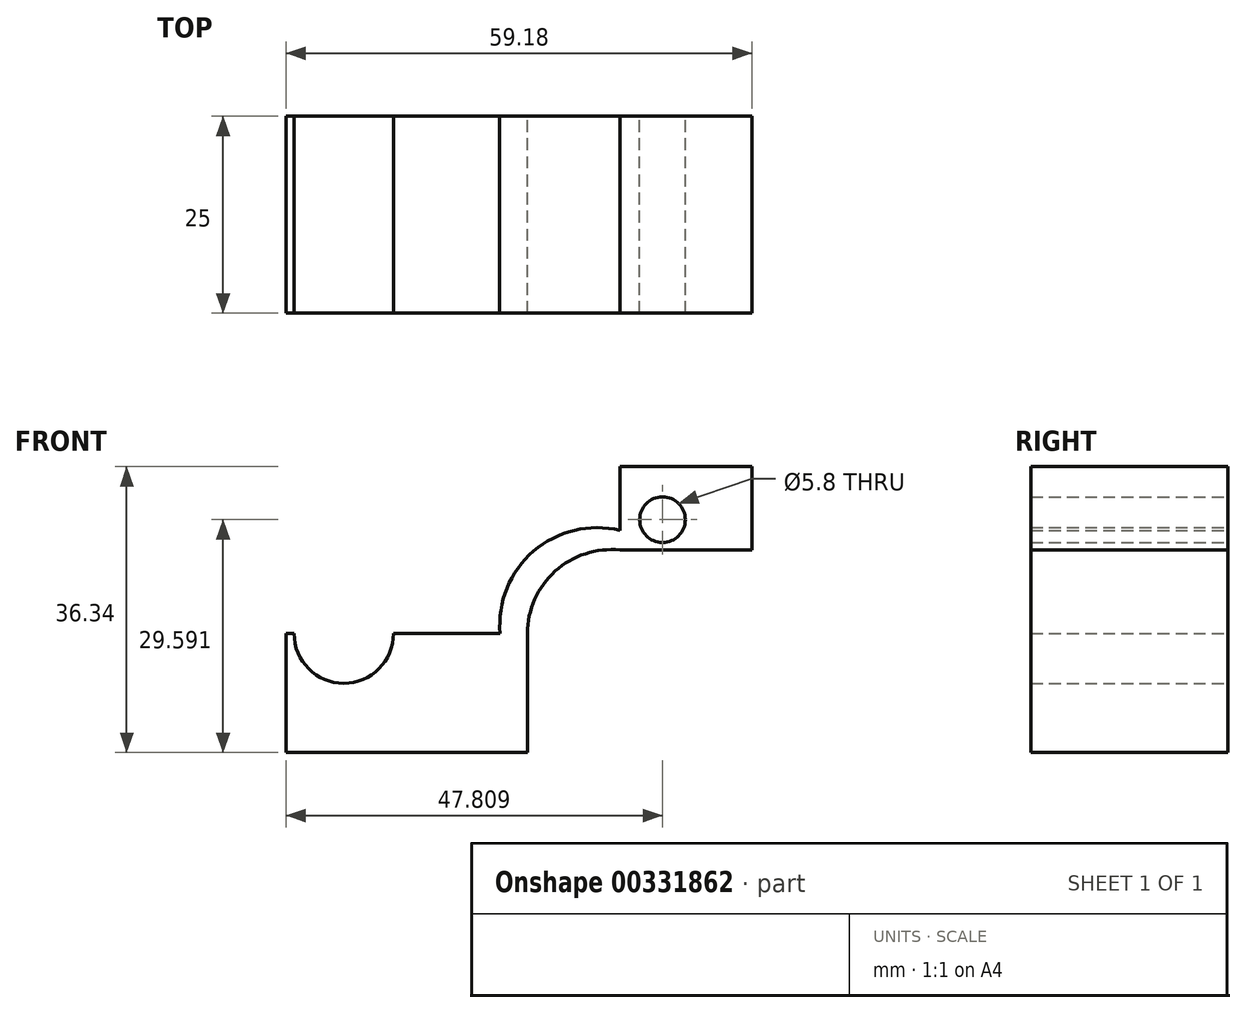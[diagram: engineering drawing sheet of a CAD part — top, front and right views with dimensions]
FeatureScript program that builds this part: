
annotation { "Feature Type Name" : "Feature", "Feature Type Description" : "" }
export const myFeature = defineFeature(function(context is Context, id is Id, definition is map)
    precondition{}
    {
        {
            var Q0;
            Q0=qCreatedBy(makeId("Front.planeOp"),FACE);
            var sketch = newSketch(context, id + "F0", { "sketchPlane" : qUnion([Q0])});
            skLineSegment(sketch, "E0.bottom", {"start": v(0, 0) * mm, "end": v(30.65, 0) * mm});
            skLineSegment(sketch, "E0.top", {"start": v(0, 15.13) * mm, "end": v(30.65, 15.13) * mm});
            skLineSegment(sketch, "E0.left", {"start": v(0, 0) * mm, "end": v(0, 15.13) * mm});
            skLineSegment(sketch, "E0.right", {"start": v(30.65, 0) * mm, "end": v(30.65, 15.13) * mm});
            skLineSegment(sketch, "E1.bottom", {"start": v(42.41, 25.74) * mm, "end": v(59.18, 25.74) * mm});
            skLineSegment(sketch, "E1.top", {"start": v(42.41, 36.34) * mm, "end": v(59.18, 36.34) * mm});
            skLineSegment(sketch, "E1.left", {"start": v(42.41, 25.74) * mm, "end": v(42.41, 36.34) * mm});
            skLineSegment(sketch, "E1.right", {"start": v(59.18, 25.74) * mm, "end": v(59.18, 36.34) * mm});
            skArc(sketch, "E2", {"start": v(42.41, 25.74) * mm, "mid": v(34.17, 23.05) * mm, "end": v(30.65, 15.13) * mm});
            skArc(sketch, "E3", {"start": v(42.41, 28.24) * mm, "mid": v(31.43, 25.6) * mm, "end": v(27.18, 15.13) * mm});
            skCircle(sketch, "E4", {"center": v(47.8, 29.6) * mm, "radius": 2.9 * mm});
            skCircle(sketch, "E5", {"center": v(7.33, 15.13) * mm, "radius": 6.31 * mm});
            skSolve(sketch);
        }
        {
            var Q0;
            {var subQ0=sQuery(id+"F0.wireOp",EDGE,"E5");var subQ1=sQuery(id+"F0.wireOp",EDGE,"E0.top");var subQ2=makeQuery(id+"F0.imprint","INTERSECT",VERTEX,{"disambiguationData":[OD(0.0)],"derivedFrom":[subQ1,subQ0]});Q0=makeQuery(id+"F0.imprint","IMPRINT",FACE,{"disambiguationData":[TD([[makeQuery(id+"F0.imprint","IMPRINT",EDGE,{"disambiguationData":[TD([[subQ2,-1.0]])],"derivedFrom":subQ1}),1.0]])]});}
            var Q1;
            {var subQ0=sQuery(id+"F0.wireOp",EDGE,"E5");var subQ1=sQuery(id+"F0.wireOp",EDGE,"E0.top");var subQ2=makeQuery(id+"F0.imprint","INTERSECT",VERTEX,{"disambiguationData":[OD(0.0)],"derivedFrom":[subQ1,subQ0]});Q1=makeQuery(id+"F0.imprint","IMPRINT",FACE,{"disambiguationData":[TD([[makeQuery(id+"F0.imprint","IMPRINT",EDGE,{"disambiguationData":[TD([[subQ2,-1.0]])],"derivedFrom":subQ1}),-1.0]])]});}
            var Q2;
            {var subQ0=sQuery(id+"F0.wireOp",EDGE,"E2");Q2=makeQuery(id+"F0.imprint","IMPRINT",FACE,{"disambiguationData":[TD([[makeQuery(id+"F0.imprint","IMPRINT",EDGE,{"derivedFrom":subQ0}),-1.0]])]});}
            var Q3;
            {var subQ3=sQuery(id+"F0.wireOp",EDGE,"E1.bottom");Q3=makeQuery(id+"F0.imprint","IMPRINT",FACE,{"disambiguationData":[TD([[makeQuery(id+"F0.imprint","IMPRINT",EDGE,{"derivedFrom":subQ3}),1.0]])]});}
            extrude(context, id + "F1", {"entities" : qUnion([Q0, Q1, Q2, Q3]), "depth" : 25 * mm});
        }
    });
